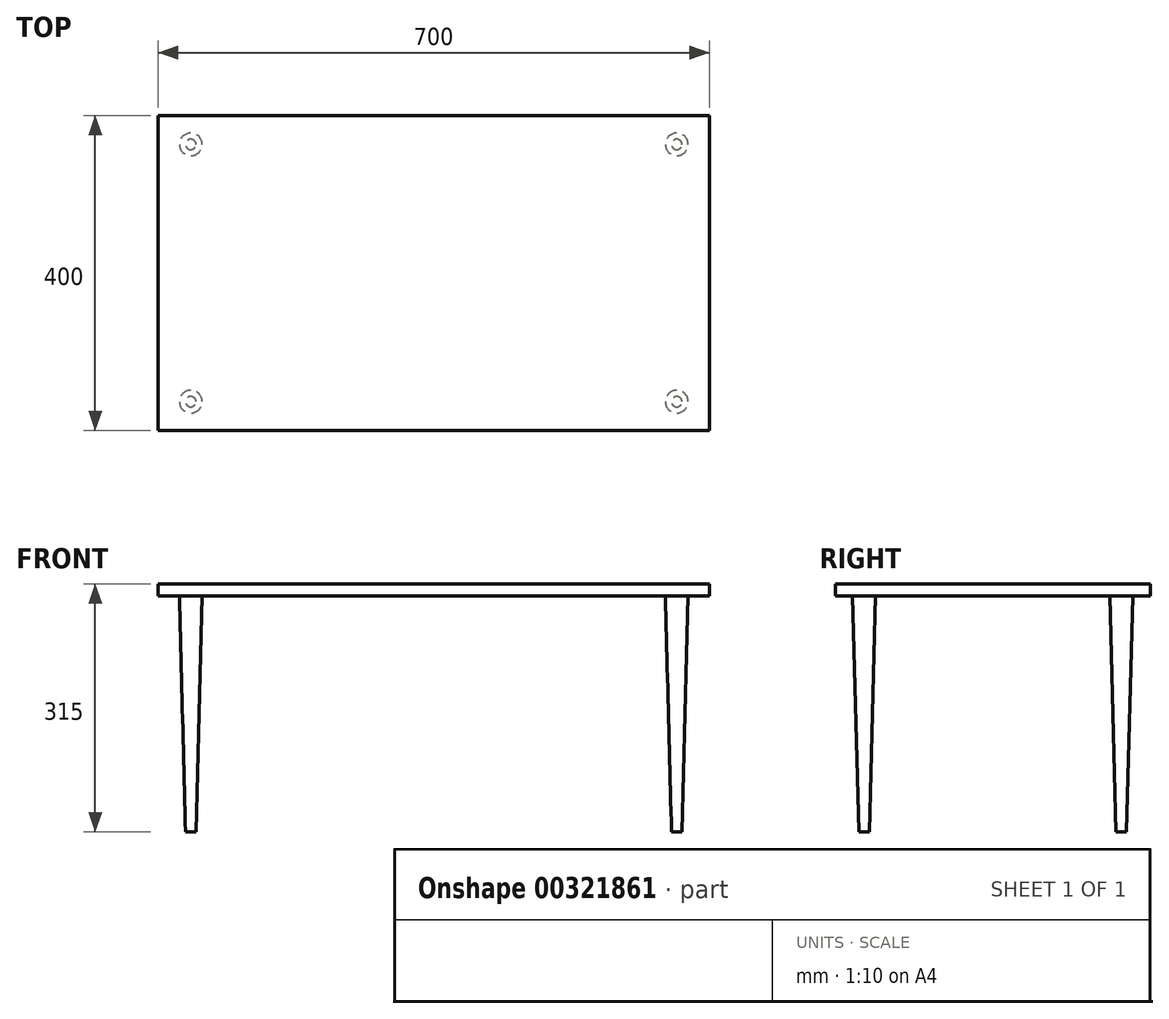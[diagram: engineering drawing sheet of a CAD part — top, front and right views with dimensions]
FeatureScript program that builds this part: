
annotation { "Feature Type Name" : "Feature", "Feature Type Description" : "" }
export const myFeature = defineFeature(function(context is Context, id is Id, definition is map)
    precondition{}
    {
        {
            var Q0;
            Q0=qCreatedBy(makeId("Top.planeOp"),FACE);
            var sketch = newSketch(context, id + "F0", { "sketchPlane" : qUnion([Q0])});
            skLineSegment(sketch, "E0.bottom", {"start": v(350, 200) * mm, "end": v(-350, 200) * mm});
            skLineSegment(sketch, "E0.top", {"start": v(350, -200) * mm, "end": v(-350, -200) * mm});
            skLineSegment(sketch, "E0.left", {"start": v(350, 200) * mm, "end": v(350, -200) * mm});
            skLineSegment(sketch, "E0.right", {"start": v(-350, 200) * mm, "end": v(-350, -200) * mm});
            skPoint(sketch, "E0.middle", {"position": v(0, 0) * mm});
            skSolve(sketch);
        }
        {
            var Q0;
            Q0=makeQuery(id+"F0.imprint","IMPRINT",FACE,{"disambiguationData":[TD([[makeQuery(id+"F0.imprint","IMPRINT",EDGE,{"derivedFrom":sQuery(id+"F0.wireOp",EDGE,"E0.bottom")}),1.0]])]});
            extrude(context, id + "F1", {"entities" : qUnion([Q0]), "oppositeDirection" : true, "depth" : 15 * mm});
        }
        {
            var Q0;
            Q0=makeQuery(id+"F1.opExtrude","CAP_FACE",FACE,{"disambiguationData":[OSD([sQuery(id+"F0.wireOp",EDGE,"E0.bottom"),sQuery(id+"F0.wireOp",EDGE,"E0.top"),sQuery(id+"F0.wireOp",EDGE,"E0.left"),sQuery(id+"F0.wireOp",EDGE,"E0.right")])],"isStart":false});
            var sketch = newSketch(context, id + "F2", { "sketchPlane" : qUnion([Q0])});
            skLineSegment(sketch, "E1", {"start": v(-350, 0) * mm, "end": v(350, 0) * mm, "construction": true});
            skLineSegment(sketch, "E2", {"start": v(0, -200) * mm, "end": v(0, 200) * mm, "construction": true});
            skCircle(sketch, "E3", {"center": v(-308.65, 163.42) * mm, "radius": 14.5 * mm});
            skCircle(sketch, "E4.MirrorC", {"center": v(-308.65, -163.42) * mm, "radius": 14.5 * mm});
            skCircle(sketch, "E5.MirrorC", {"center": v(308.65, 163.42) * mm, "radius": 14.5 * mm});
            skCircle(sketch, "E6.MirrorC", {"center": v(308.65, -163.42) * mm, "radius": 14.5 * mm});
            skSolve(sketch);
        }
        {
            var Q0;
            Q0 = qSketchRegion(id + "F2", true);
            extrude(context, id + "F3", {"entities" : qUnion([Q0]), "operationType" : NewBodyOperationType.ADD, "depth" : 300 * mm, "hasDraft" : true, "draftAngle" : 1.5 * degree, "draftPullDirection" : true});
        }
    });
